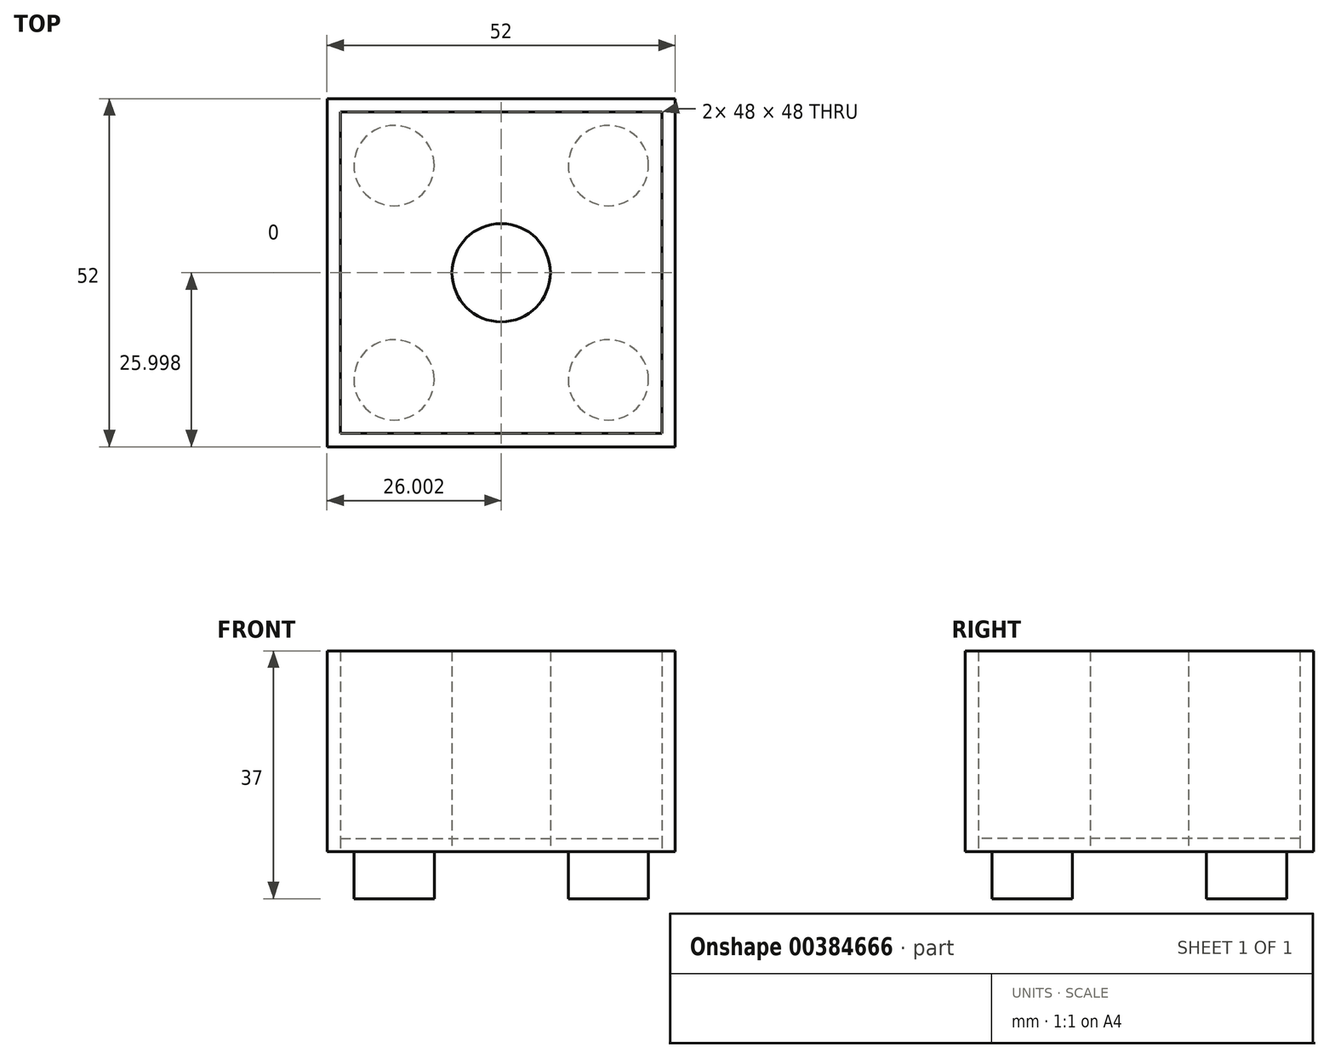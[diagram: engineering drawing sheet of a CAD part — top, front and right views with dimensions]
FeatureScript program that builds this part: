
annotation { "Feature Type Name" : "Feature", "Feature Type Description" : "" }
export const myFeature = defineFeature(function(context is Context, id is Id, definition is map)
    precondition{}
    {
        {
            var Q0;
            Q0=qCreatedBy(makeId("Top.planeOp"),FACE);
            var sketch = newSketch(context, id + "F0", { "sketchPlane" : qUnion([Q0])});
            skLineSegment(sketch, "E0.bottom", {"start": v(-29.29, 24.26) * mm, "end": v(22.71, 24.26) * mm});
            skLineSegment(sketch, "E0.top", {"start": v(-29.29, -27.74) * mm, "end": v(22.71, -27.74) * mm});
            skLineSegment(sketch, "E0.left", {"start": v(-29.29, 24.26) * mm, "end": v(-29.29, -27.74) * mm});
            skLineSegment(sketch, "E0.right", {"start": v(22.71, 24.26) * mm, "end": v(22.71, -27.74) * mm});
            skCircle(sketch, "E1", {"center": v(-19.29, 14.26) * mm, "radius": 6 * mm});
            skCircle(sketch, "E2", {"center": v(12.71, 14.26) * mm, "radius": 6 * mm});
            skCircle(sketch, "E3", {"center": v(-19.29, -17.74) * mm, "radius": 6 * mm});
            skCircle(sketch, "E4", {"center": v(12.71, -17.74) * mm, "radius": 6 * mm});
            skLineSegment(sketch, "E5.0", {"start": v(-19.29, 14.26) * mm, "end": v(12.71, 14.26) * mm});
            skLineSegment(sketch, "E5.1", {"start": v(-19.29, 14.26) * mm, "end": v(-19.29, -17.74) * mm});
            skLineSegment(sketch, "E5.2", {"start": v(-19.29, -17.74) * mm, "end": v(12.71, -17.74) * mm});
            skLineSegment(sketch, "E5.3", {"start": v(12.71, 14.26) * mm, "end": v(12.71, -17.74) * mm});
            skCircle(sketch, "E6", {"center": v(-3.29, -1.74) * mm, "radius": 7.34 * mm});
            skPoint(sketch, "E6.centerSnap0", {"position": v(-3.29, 24.26) * mm});
            skPoint(sketch, "E6.centerSnap1", {"position": v(-29.29, -1.74) * mm});
            skLineSegment(sketch, "E7.0", {"start": v(-27.29, 22.26) * mm, "end": v(20.71, 22.26) * mm});
            skLineSegment(sketch, "E7.1", {"start": v(-27.29, 22.26) * mm, "end": v(-27.29, -25.74) * mm});
            skLineSegment(sketch, "E7.2", {"start": v(-27.29, -25.74) * mm, "end": v(20.71, -25.74) * mm});
            skLineSegment(sketch, "E7.3", {"start": v(20.71, 22.26) * mm, "end": v(20.71, -25.74) * mm});
            skSolve(sketch);
        }
        {
            var Q0;
            Q0=makeQuery(id+"F0.imprint","IMPRINT",FACE,{"disambiguationData":[TD([[makeQuery(id+"F0.imprint","IMPRINT",EDGE,{"derivedFrom":sQuery(id+"F0.wireOp",EDGE,"E0.bottom")}),-1.0]])]});
            var Q1;
            Q1=makeQuery(id+"F0.imprint","IMPRINT",FACE,{"disambiguationData":[TD([[makeQuery(id+"F0.imprint","IMPRINT",EDGE,{"derivedFrom":sQuery(id+"F0.wireOp",EDGE,"E6")}),1.0]])]});
            extrude(context, id + "F1", {"entities" : qUnion([Q0, Q1]), "depth" : 30 * mm});
        }
        {
            var Q0;
            {var subQ0=sQuery(id+"F0.wireOp",EDGE,"E5.0");var subQ1=sQuery(id+"F0.wireOp",EDGE,"E2");var subQ2=makeQuery(id+"F0.imprint","INTERSECT",VERTEX,{"derivedFrom":[subQ1,subQ0]});Q0=makeQuery(id+"F0.imprint","IMPRINT",FACE,{"disambiguationData":[TD([[makeQuery(id+"F0.imprint","IMPRINT",EDGE,{"disambiguationData":[TD([[subQ2,1.0]])],"derivedFrom":subQ1}),1.0]])]});}
            var Q1;
            {var subQ0=sQuery(id+"F0.wireOp",EDGE,"E5.0");var subQ1=sQuery(id+"F0.wireOp",EDGE,"E2");var subQ2=makeQuery(id+"F0.imprint","INTERSECT",VERTEX,{"derivedFrom":[subQ1,subQ0]});Q1=makeQuery(id+"F0.imprint","IMPRINT",FACE,{"disambiguationData":[TD([[makeQuery(id+"F0.imprint","IMPRINT",EDGE,{"disambiguationData":[TD([[subQ2,-1.0]])],"derivedFrom":subQ1}),1.0]])]});}
            var Q2;
            {var subQ0=sQuery(id+"F0.wireOp",EDGE,"E5.0");var subQ1=sQuery(id+"F0.wireOp",EDGE,"E1");var subQ2=makeQuery(id+"F0.imprint","INTERSECT",VERTEX,{"derivedFrom":[subQ1,subQ0]});Q2=makeQuery(id+"F0.imprint","IMPRINT",FACE,{"disambiguationData":[TD([[makeQuery(id+"F0.imprint","IMPRINT",EDGE,{"disambiguationData":[TD([[subQ2,-1.0]])],"derivedFrom":subQ1}),1.0]])]});}
            var Q3;
            {var subQ0=sQuery(id+"F0.wireOp",EDGE,"E5.0");var subQ1=sQuery(id+"F0.wireOp",EDGE,"E1");var subQ2=makeQuery(id+"F0.imprint","INTERSECT",VERTEX,{"derivedFrom":[subQ1,subQ0]});Q3=makeQuery(id+"F0.imprint","IMPRINT",FACE,{"disambiguationData":[TD([[makeQuery(id+"F0.imprint","IMPRINT",EDGE,{"disambiguationData":[TD([[subQ2,1.0]])],"derivedFrom":subQ1}),1.0]])]});}
            var Q4;
            {var subQ0=sQuery(id+"F0.wireOp",EDGE,"E5.2");var subQ1=sQuery(id+"F0.wireOp",EDGE,"E4");var subQ2=makeQuery(id+"F0.imprint","INTERSECT",VERTEX,{"derivedFrom":[subQ1,subQ0]});Q4=makeQuery(id+"F0.imprint","IMPRINT",FACE,{"disambiguationData":[TD([[makeQuery(id+"F0.imprint","IMPRINT",EDGE,{"disambiguationData":[TD([[subQ2,-1.0]])],"derivedFrom":subQ1}),1.0]])]});}
            var Q5;
            {var subQ0=sQuery(id+"F0.wireOp",EDGE,"E5.2");var subQ1=sQuery(id+"F0.wireOp",EDGE,"E4");var subQ2=makeQuery(id+"F0.imprint","INTERSECT",VERTEX,{"derivedFrom":[subQ1,subQ0]});Q5=makeQuery(id+"F0.imprint","IMPRINT",FACE,{"disambiguationData":[TD([[makeQuery(id+"F0.imprint","IMPRINT",EDGE,{"disambiguationData":[TD([[subQ2,1.0]])],"derivedFrom":subQ1}),1.0]])]});}
            var Q6;
            {var subQ0=sQuery(id+"F0.wireOp",EDGE,"E5.1");var subQ1=sQuery(id+"F0.wireOp",EDGE,"E3");var subQ2=makeQuery(id+"F0.imprint","INTERSECT",VERTEX,{"derivedFrom":[subQ1,subQ0]});Q6=makeQuery(id+"F0.imprint","IMPRINT",FACE,{"disambiguationData":[TD([[makeQuery(id+"F0.imprint","IMPRINT",EDGE,{"disambiguationData":[TD([[subQ2,1.0]])],"derivedFrom":subQ1}),1.0]])]});}
            var Q7;
            {var subQ0=sQuery(id+"F0.wireOp",EDGE,"E5.1");var subQ1=sQuery(id+"F0.wireOp",EDGE,"E3");var subQ2=makeQuery(id+"F0.imprint","INTERSECT",VERTEX,{"derivedFrom":[subQ1,subQ0]});Q7=makeQuery(id+"F0.imprint","IMPRINT",FACE,{"disambiguationData":[TD([[makeQuery(id+"F0.imprint","IMPRINT",EDGE,{"disambiguationData":[TD([[subQ2,-1.0]])],"derivedFrom":subQ1}),1.0]])]});}
            extrude(context, id + "F2", {"entities" : qUnion([Q0, Q1, Q2, Q3, Q4, Q5, Q6, Q7]), "oppositeDirection" : true, "depth" : 7 * mm});
        }
        {
            var Q0;
            Q0=makeQuery(id+"F0.imprint","IMPRINT",FACE,{"disambiguationData":[TD([[makeQuery(id+"F0.imprint","IMPRINT",EDGE,{"derivedFrom":sQuery(id+"F0.wireOp",EDGE,"E7.0")}),-1.0]])]});
            var Q1;
            {var subQ0=sQuery(id+"F0.wireOp",EDGE,"E5.1");var subQ1=sQuery(id+"F0.wireOp",EDGE,"E3");var subQ2=makeQuery(id+"F0.imprint","INTERSECT",VERTEX,{"derivedFrom":[subQ1,subQ0]});Q1=makeQuery(id+"F0.imprint","IMPRINT",FACE,{"disambiguationData":[TD([[makeQuery(id+"F0.imprint","IMPRINT",EDGE,{"disambiguationData":[TD([[subQ2,1.0]])],"derivedFrom":subQ1}),1.0]])]});}
            var Q2;
            {var subQ0=sQuery(id+"F0.wireOp",EDGE,"E5.1");var subQ1=sQuery(id+"F0.wireOp",EDGE,"E3");var subQ2=makeQuery(id+"F0.imprint","INTERSECT",VERTEX,{"derivedFrom":[subQ1,subQ0]});Q2=makeQuery(id+"F0.imprint","IMPRINT",FACE,{"disambiguationData":[TD([[makeQuery(id+"F0.imprint","IMPRINT",EDGE,{"disambiguationData":[TD([[subQ2,-1.0]])],"derivedFrom":subQ1}),1.0]])]});}
            var Q3;
            Q3=makeQuery(id+"F0.imprint","IMPRINT",FACE,{"disambiguationData":[TD([[makeQuery(id+"F0.imprint","IMPRINT",EDGE,{"derivedFrom":sQuery(id+"F0.wireOp",EDGE,"E6")}),-1.0]])]});
            var Q4;
            {var subQ0=sQuery(id+"F0.wireOp",EDGE,"E5.0");var subQ1=sQuery(id+"F0.wireOp",EDGE,"E1");var subQ2=makeQuery(id+"F0.imprint","INTERSECT",VERTEX,{"derivedFrom":[subQ1,subQ0]});Q4=makeQuery(id+"F0.imprint","IMPRINT",FACE,{"disambiguationData":[TD([[makeQuery(id+"F0.imprint","IMPRINT",EDGE,{"disambiguationData":[TD([[subQ2,-1.0]])],"derivedFrom":subQ1}),1.0]])]});}
            var Q5;
            {var subQ0=sQuery(id+"F0.wireOp",EDGE,"E5.0");var subQ1=sQuery(id+"F0.wireOp",EDGE,"E1");var subQ2=makeQuery(id+"F0.imprint","INTERSECT",VERTEX,{"derivedFrom":[subQ1,subQ0]});Q5=makeQuery(id+"F0.imprint","IMPRINT",FACE,{"disambiguationData":[TD([[makeQuery(id+"F0.imprint","IMPRINT",EDGE,{"disambiguationData":[TD([[subQ2,1.0]])],"derivedFrom":subQ1}),1.0]])]});}
            var Q6;
            {var subQ0=sQuery(id+"F0.wireOp",EDGE,"E5.0");var subQ1=sQuery(id+"F0.wireOp",EDGE,"E2");var subQ2=makeQuery(id+"F0.imprint","INTERSECT",VERTEX,{"derivedFrom":[subQ1,subQ0]});Q6=makeQuery(id+"F0.imprint","IMPRINT",FACE,{"disambiguationData":[TD([[makeQuery(id+"F0.imprint","IMPRINT",EDGE,{"disambiguationData":[TD([[subQ2,1.0]])],"derivedFrom":subQ1}),1.0]])]});}
            var Q7;
            {var subQ0=sQuery(id+"F0.wireOp",EDGE,"E5.0");var subQ1=sQuery(id+"F0.wireOp",EDGE,"E2");var subQ2=makeQuery(id+"F0.imprint","INTERSECT",VERTEX,{"derivedFrom":[subQ1,subQ0]});Q7=makeQuery(id+"F0.imprint","IMPRINT",FACE,{"disambiguationData":[TD([[makeQuery(id+"F0.imprint","IMPRINT",EDGE,{"disambiguationData":[TD([[subQ2,-1.0]])],"derivedFrom":subQ1}),1.0]])]});}
            var Q8;
            {var subQ0=sQuery(id+"F0.wireOp",EDGE,"E5.2");var subQ1=sQuery(id+"F0.wireOp",EDGE,"E4");var subQ2=makeQuery(id+"F0.imprint","INTERSECT",VERTEX,{"derivedFrom":[subQ1,subQ0]});Q8=makeQuery(id+"F0.imprint","IMPRINT",FACE,{"disambiguationData":[TD([[makeQuery(id+"F0.imprint","IMPRINT",EDGE,{"disambiguationData":[TD([[subQ2,1.0]])],"derivedFrom":subQ1}),1.0]])]});}
            var Q9;
            {var subQ0=sQuery(id+"F0.wireOp",EDGE,"E5.2");var subQ1=sQuery(id+"F0.wireOp",EDGE,"E4");var subQ2=makeQuery(id+"F0.imprint","INTERSECT",VERTEX,{"derivedFrom":[subQ1,subQ0]});Q9=makeQuery(id+"F0.imprint","IMPRINT",FACE,{"disambiguationData":[TD([[makeQuery(id+"F0.imprint","IMPRINT",EDGE,{"disambiguationData":[TD([[subQ2,-1.0]])],"derivedFrom":subQ1}),1.0]])]});}
            var Q10;
            Q10=makeQuery(id+"F0.imprint","IMPRINT",FACE,{"disambiguationData":[TD([[makeQuery(id+"F0.imprint","IMPRINT",EDGE,{"derivedFrom":sQuery(id+"F0.wireOp",EDGE,"E6")}),1.0]])]});
            extrude(context, id + "F3", {"entities" : qUnion([Q0, Q1, Q2, Q3, Q4, Q5, Q6, Q7, Q8, Q9, Q10]), "depth" : 2 * mm});
        }
    });
